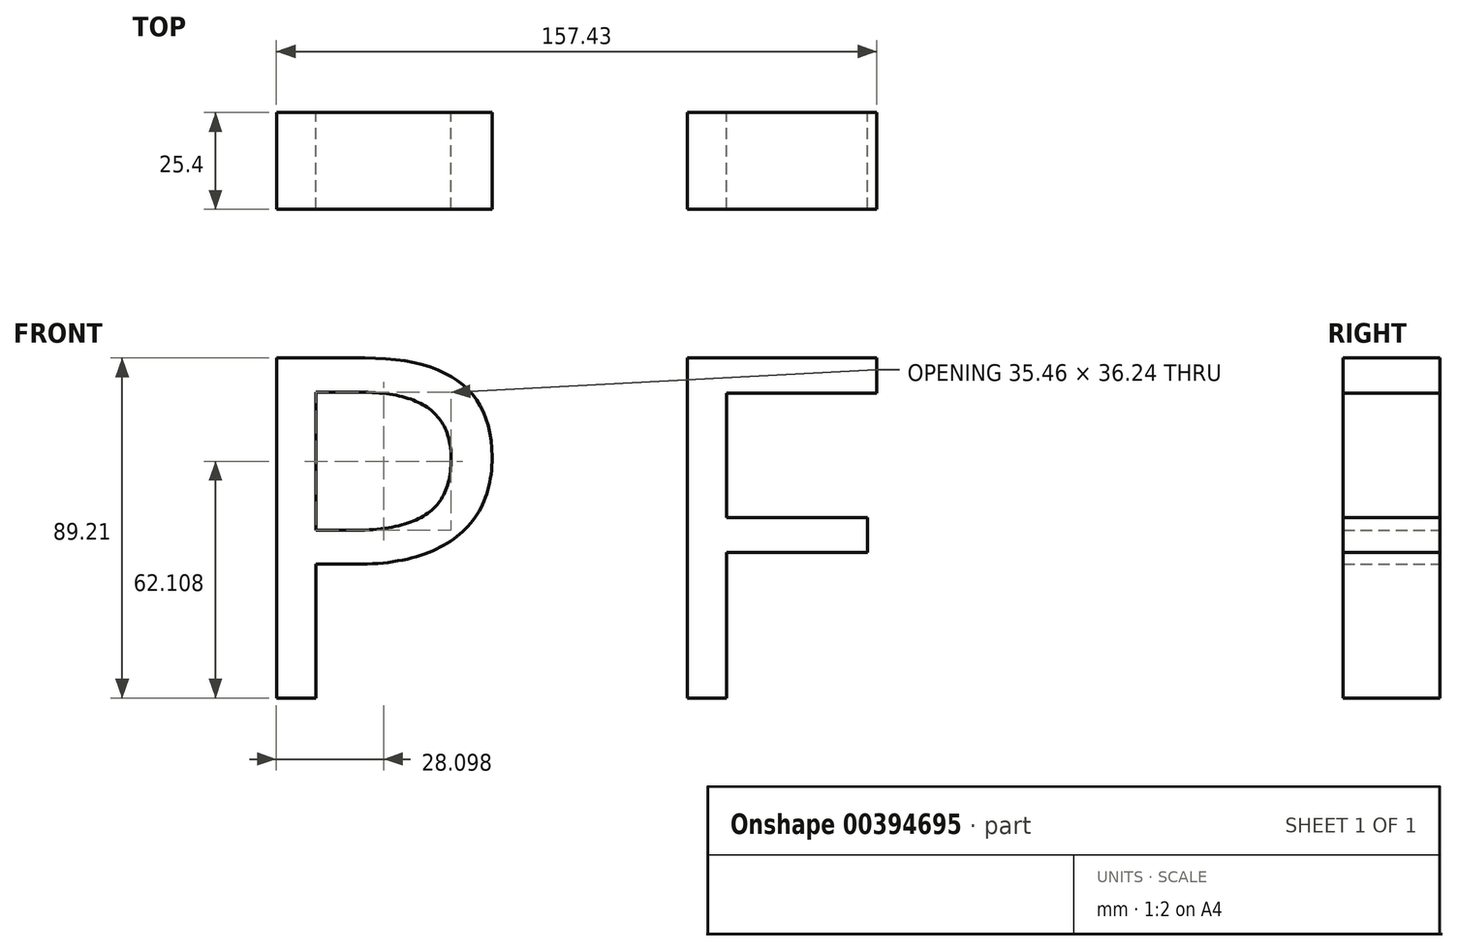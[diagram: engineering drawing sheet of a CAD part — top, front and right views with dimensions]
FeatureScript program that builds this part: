
annotation { "Feature Type Name" : "Feature", "Feature Type Description" : "" }
export const myFeature = defineFeature(function(context is Context, id is Id, definition is map)
    precondition{}
    {
        {
            var Q0;
            Q0=qCreatedBy(makeId("Front.planeOp"),FACE);
            var sketch = newSketch(context, id + "F0", { "sketchPlane" : qUnion([Q0])});
            skText(sketch, "E0", { "text": "P F", "fontName": "OpenSans-Regular.ttf"});
            const initialGuessF0  = {"E0": [-0.0606, -0.05466, 1, 0, 0.08997]};
            skSetInitialGuess(sketch, initialGuessF0);
            skSolve(sketch);
        }
        {
            var Q0;
            Q0 = qSketchRegion(id + "F0", true);
            extrude(context, id + "F1", {"entities" : qUnion([Q0]), "depth" : 25.4 * mm});
        }
    });
